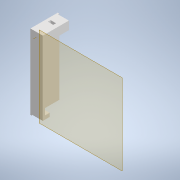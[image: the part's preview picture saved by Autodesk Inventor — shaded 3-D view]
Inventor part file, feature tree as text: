
AUTODESK INVENTOR PART (.ipt)
format: ipt  version: 2021 (Build 250183000, 183)  size: 177,152 bytes
history: native  units: mm
features: reference x11, extrude x8, sketch x8, other x4, plane x1
ambient origin geometry x8: Origin, YZ Plane, XZ Plane, XY Plane, X Axis, Y Axis, Z Axis, Center Point
bodies: Solid1 (feature_tree)
feature tree (32):
  plane  "Work Plane1"
  extrude  "Extrusion1"  Depth=2.4mm TaperAngle=0.0deg
  extrude  "Extrusion2"  Depth=26.2mm TaperAngle=0.0deg
  extrude  "Extrusion3"  Depth=5.0mm TaperAngle=0.0deg
  extrude  "Extrusion4"  Depth=1.6mm TaperAngle=0.0deg
  extrude  "Extrusion5"  Depth=3.0mm
  extrude  "Extrusion6"  Depth=4.0mm
  extrude  "Extrusion7"  Depth=3.0mm
  other  "Work Axis1"
  extrude  "Extrusion8"  Depth=11.0mm
  sketch  "Sketch1"  dims[d0=1.6mm d1=2.4mm d2=0.0mm]
  reference  "Reference1"
  reference  "Reference2"
  reference  "Reference3"
  sketch  "Sketch2"  dims[d3=0.4mm d4=26.2mm d5=0.0mm]
  reference  "Reference4"
  reference  "Reference5"
  sketch  "Sketch3"  dims[d6=4.0mm d7=5.0mm d8=0.0mm]
  sketch  "Sketch4"  dims[d9=8.0mm d10=1.6mm d11=0.0mm]
  reference  "Reference6"
  reference  "Reference7"
  sketch  "Sketch5"  dims[d12=1.6mm d13=0.0mm d14=3.0mm]
  reference  "Reference8"
  reference  "Reference9"
  sketch  "Sketch6"  dims[d15=1.6mm d16=0.0mm d17=4.0mm]
  reference  "Reference10"
  sketch  "Sketch7"  dims[d18=12.0mm d19=0.0mm d23=3.0mm]
  reference  "Reference11"
  sketch  "Sketch9"  dims[d24=6.0mm d25=11.0mm d26=3.0mm d27=0.0mm d28=0.0mm]
  parser-record x1  (decoder bookkeeping rows leaked as tree rows — omitted from the tree; the rows remain in map.json)
  other  "Assembly.iam"
  other  "LRS-50-Series(MW):1"
note: 1 file-system path scrubbed to <path> (originals preserved in map.json)
